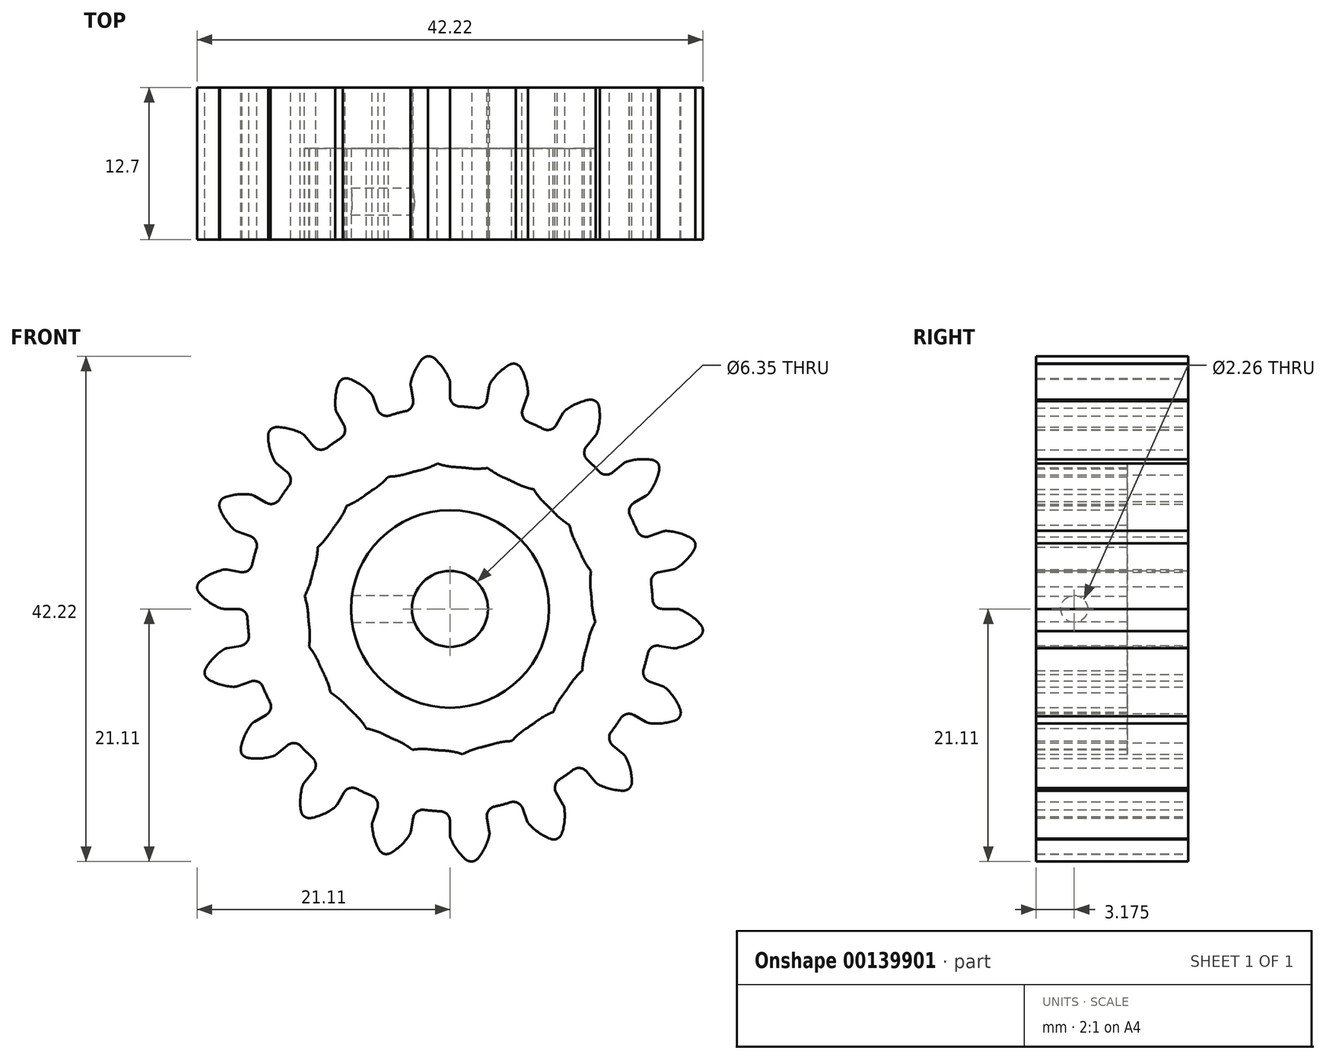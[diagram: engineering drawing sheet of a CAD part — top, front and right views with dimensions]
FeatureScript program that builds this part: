
annotation { "Feature Type Name" : "Feature", "Feature Type Description" : "" }
export const myFeature = defineFeature(function(context is Context, id is Id, definition is map)
    precondition{}
    {
        {
            var Q0;
            Q0=qCreatedBy(makeId("Front.planeOp"),FACE);
            var sketch = newSketch(context, id + "F0", { "sketchPlane" : qUnion([Q0])});
            skArc(sketch, "E0", {"start": v(-3.71, 16.52) * mm, "mid": v(-4.38, 16.35) * mm, "end": v(-5.04, 16.16) * mm});
            skArc(sketch, "E1", {"start": v(-0.07, 19.21) * mm, "mid": v(-0.58, 20.13) * mm, "end": v(-1.28, 20.9) * mm});
            skLineSegment(sketch, "E2", {"start": v(0, 18.89) * mm, "end": v(0, 17.74) * mm});
            skLineSegment(sketch, "E3", {"start": v(-1.83, 21.11) * mm, "end": v(-1.85, 21.11) * mm});
            skLineSegment(sketch, "E4.MirrorCS", {"start": v(-1.86, 21.1) * mm, "end": v(-1.85, 21.11) * mm});
            skArc(sketch, "E5.MirrorCS", {"start": v(-3.27, 18.93) * mm, "mid": v(-2.92, 19.92) * mm, "end": v(-2.37, 20.8) * mm});
            skLineSegment(sketch, "E6.MirrorCS", {"start": v(-3.28, 18.6) * mm, "end": v(-3.08, 17.47) * mm});
            skPoint(sketch, "E7.visualSharp", {"position": v(0, 16.93) * mm});
            skArc(sketch, "E7.filletArc", {"start": v(0, 17.74) * mm, "mid": v(0.23, 17.17) * mm, "end": v(0.79, 16.91) * mm});
            skPoint(sketch, "E8.visualSharp", {"position": v(-2.94, 16.67) * mm});
            skArc(sketch, "E8.filletArc", {"start": v(-3.71, 16.52) * mm, "mid": v(-3.2, 16.86) * mm, "end": v(-3.08, 17.47) * mm});
            skPoint(sketch, "E9.visualSharp", {"position": v(-3.3, 18.76) * mm});
            skArc(sketch, "E9.filletArc", {"start": v(-3.27, 18.93) * mm, "mid": v(-3.3, 18.77) * mm, "end": v(-3.28, 18.6) * mm});
            skPoint(sketch, "E10.visualSharp", {"position": v(0, 19.05) * mm});
            skArc(sketch, "E10.filletArc", {"start": v(0, 18.89) * mm, "mid": v(-0.02, 19.05) * mm, "end": v(-0.07, 19.21) * mm});
            skPoint(sketch, "E11.visualSharp", {"position": v(-2.15, 21.06) * mm});
            skArc(sketch, "E11.filletArc", {"start": v(-1.86, 21.1) * mm, "mid": v(-2.14, 21) * mm, "end": v(-2.37, 20.8) * mm});
            skPoint(sketch, "E12.visualSharp", {"position": v(-1.53, 21.11) * mm});
            skArc(sketch, "E12.filletArc", {"start": v(-1.28, 20.9) * mm, "mid": v(-1.54, 21.06) * mm, "end": v(-1.83, 21.11) * mm});
            skArc(sketch, "E13.1.0", {"start": v(-9.14, 14.25) * mm, "mid": v(-8.78, 14.75) * mm, "end": v(-8.87, 15.36) * mm});
            skLineSegment(sketch, "E13.1.1", {"start": v(-9.44, 16.36) * mm, "end": v(-8.87, 15.36) * mm});
            skArc(sketch, "E13.1.2", {"start": v(-9.55, 16.67) * mm, "mid": v(-9.51, 16.51) * mm, "end": v(-9.44, 16.36) * mm});
            skArc(sketch, "E13.1.3", {"start": v(-9.55, 16.67) * mm, "mid": v(-9.56, 17.72) * mm, "end": v(-9.34, 18.74) * mm});
            skArc(sketch, "E13.1.4", {"start": v(-8.97, 19.2) * mm, "mid": v(-9.2, 19) * mm, "end": v(-9.34, 18.74) * mm});
            skLineSegment(sketch, "E13.1.5", {"start": v(-8.97, 19.2) * mm, "end": v(-8.96, 19.2) * mm});
            skLineSegment(sketch, "E13.1.6", {"start": v(-8.94, 19.21) * mm, "end": v(-8.96, 19.2) * mm});
            skArc(sketch, "E13.1.7", {"start": v(-8.35, 19.2) * mm, "mid": v(-8.65, 19.26) * mm, "end": v(-8.94, 19.21) * mm});
            skArc(sketch, "E13.1.8", {"start": v(-6.63, 18.03) * mm, "mid": v(-7.43, 18.71) * mm, "end": v(-8.35, 19.2) * mm});
            skArc(sketch, "E13.1.9", {"start": v(-6.46, 17.75) * mm, "mid": v(-6.53, 17.9) * mm, "end": v(-6.63, 18.03) * mm});
            skLineSegment(sketch, "E13.1.10", {"start": v(-6.46, 17.75) * mm, "end": v(-6.07, 16.67) * mm});
            skArc(sketch, "E13.1.11", {"start": v(-6.07, 16.67) * mm, "mid": v(-5.66, 16.2) * mm, "end": v(-5.04, 16.16) * mm});
            skArc(sketch, "E13.2.0", {"start": v(-13.46, 10.27) * mm, "mid": v(-13.3, 10.86) * mm, "end": v(-13.59, 11.4) * mm});
            skLineSegment(sketch, "E13.2.1", {"start": v(-14.47, 12.14) * mm, "end": v(-13.59, 11.4) * mm});
            skArc(sketch, "E13.2.2", {"start": v(-14.68, 12.4) * mm, "mid": v(-14.59, 12.26) * mm, "end": v(-14.47, 12.14) * mm});
            skArc(sketch, "E13.2.3", {"start": v(-14.68, 12.4) * mm, "mid": v(-15.04, 13.38) * mm, "end": v(-15.19, 14.42) * mm});
            skArc(sketch, "E13.2.4", {"start": v(-15, 14.97) * mm, "mid": v(-15.14, 14.71) * mm, "end": v(-15.19, 14.42) * mm});
            skLineSegment(sketch, "E13.2.5", {"start": v(-15, 14.97) * mm, "end": v(-14.98, 14.98) * mm});
            skLineSegment(sketch, "E13.2.6", {"start": v(-14.97, 15) * mm, "end": v(-14.98, 14.98) * mm});
            skArc(sketch, "E13.2.7", {"start": v(-14.42, 15.19) * mm, "mid": v(-14.71, 15.14) * mm, "end": v(-14.97, 15) * mm});
            skArc(sketch, "E13.2.8", {"start": v(-12.4, 14.68) * mm, "mid": v(-13.38, 15.04) * mm, "end": v(-14.42, 15.19) * mm});
            skArc(sketch, "E13.2.9", {"start": v(-12.14, 14.47) * mm, "mid": v(-12.26, 14.59) * mm, "end": v(-12.4, 14.68) * mm});
            skLineSegment(sketch, "E13.2.10", {"start": v(-12.14, 14.47) * mm, "end": v(-11.4, 13.59) * mm});
            skArc(sketch, "E13.2.11", {"start": v(-11.4, 13.59) * mm, "mid": v(-10.86, 13.3) * mm, "end": v(-10.27, 13.46) * mm});
            skArc(sketch, "E13.3.0", {"start": v(-16.16, 5.04) * mm, "mid": v(-16.2, 5.66) * mm, "end": v(-16.67, 6.07) * mm});
            skLineSegment(sketch, "E13.3.1", {"start": v(-17.75, 6.46) * mm, "end": v(-16.67, 6.07) * mm});
            skArc(sketch, "E13.3.2", {"start": v(-18.03, 6.63) * mm, "mid": v(-17.9, 6.53) * mm, "end": v(-17.75, 6.46) * mm});
            skArc(sketch, "E13.3.3", {"start": v(-18.03, 6.63) * mm, "mid": v(-18.71, 7.43) * mm, "end": v(-19.2, 8.35) * mm});
            skArc(sketch, "E13.3.4", {"start": v(-19.21, 8.94) * mm, "mid": v(-19.26, 8.65) * mm, "end": v(-19.2, 8.35) * mm});
            skLineSegment(sketch, "E13.3.5", {"start": v(-19.21, 8.94) * mm, "end": v(-19.2, 8.96) * mm});
            skLineSegment(sketch, "E13.3.6", {"start": v(-19.2, 8.97) * mm, "end": v(-19.2, 8.96) * mm});
            skArc(sketch, "E13.3.7", {"start": v(-18.74, 9.34) * mm, "mid": v(-19, 9.2) * mm, "end": v(-19.2, 8.97) * mm});
            skArc(sketch, "E13.3.8", {"start": v(-16.67, 9.55) * mm, "mid": v(-17.72, 9.56) * mm, "end": v(-18.74, 9.34) * mm});
            skArc(sketch, "E13.3.9", {"start": v(-16.36, 9.44) * mm, "mid": v(-16.51, 9.51) * mm, "end": v(-16.67, 9.55) * mm});
            skLineSegment(sketch, "E13.3.10", {"start": v(-16.36, 9.44) * mm, "end": v(-15.36, 8.87) * mm});
            skArc(sketch, "E13.3.11", {"start": v(-15.36, 8.87) * mm, "mid": v(-14.75, 8.78) * mm, "end": v(-14.25, 9.14) * mm});
            skArc(sketch, "E13.4.0", {"start": v(-16.91, -0.79) * mm, "mid": v(-17.17, -0.23) * mm, "end": v(-17.74, 0) * mm});
            skLineSegment(sketch, "E13.4.1", {"start": v(-18.89, 0) * mm, "end": v(-17.74, 0) * mm});
            skArc(sketch, "E13.4.2", {"start": v(-19.21, 0.07) * mm, "mid": v(-19.05, 0.02) * mm, "end": v(-18.89, 0) * mm});
            skArc(sketch, "E13.4.3", {"start": v(-19.21, 0.07) * mm, "mid": v(-20.13, 0.58) * mm, "end": v(-20.9, 1.28) * mm});
            skArc(sketch, "E13.4.4", {"start": v(-21.11, 1.83) * mm, "mid": v(-21.06, 1.54) * mm, "end": v(-20.9, 1.28) * mm});
            skLineSegment(sketch, "E13.4.5", {"start": v(-21.11, 1.83) * mm, "end": v(-21.11, 1.85) * mm});
            skLineSegment(sketch, "E13.4.6", {"start": v(-21.1, 1.86) * mm, "end": v(-21.11, 1.85) * mm});
            skArc(sketch, "E13.4.7", {"start": v(-20.8, 2.37) * mm, "mid": v(-21, 2.14) * mm, "end": v(-21.1, 1.86) * mm});
            skArc(sketch, "E13.4.8", {"start": v(-18.93, 3.27) * mm, "mid": v(-19.92, 2.92) * mm, "end": v(-20.8, 2.37) * mm});
            skArc(sketch, "E13.4.9", {"start": v(-18.6, 3.28) * mm, "mid": v(-18.77, 3.3) * mm, "end": v(-18.93, 3.27) * mm});
            skLineSegment(sketch, "E13.4.10", {"start": v(-18.6, 3.28) * mm, "end": v(-17.47, 3.08) * mm});
            skArc(sketch, "E13.4.11", {"start": v(-17.47, 3.08) * mm, "mid": v(-16.86, 3.2) * mm, "end": v(-16.52, 3.71) * mm});
            skArc(sketch, "E13.5.0", {"start": v(-15.62, -6.52) * mm, "mid": v(-16.05, -6.09) * mm, "end": v(-16.67, -6.07) * mm});
            skLineSegment(sketch, "E13.5.1", {"start": v(-17.75, -6.46) * mm, "end": v(-16.67, -6.07) * mm});
            skArc(sketch, "E13.5.2", {"start": v(-18.08, -6.5) * mm, "mid": v(-17.91, -6.5) * mm, "end": v(-17.75, -6.46) * mm});
            skArc(sketch, "E13.5.3", {"start": v(-18.08, -6.5) * mm, "mid": v(-19.11, -6.34) * mm, "end": v(-20.08, -5.94) * mm});
            skArc(sketch, "E13.5.4", {"start": v(-20.46, -5.5) * mm, "mid": v(-20.31, -5.76) * mm, "end": v(-20.08, -5.94) * mm});
            skLineSegment(sketch, "E13.5.5", {"start": v(-20.46, -5.5) * mm, "end": v(-20.47, -5.48) * mm});
            skLineSegment(sketch, "E13.5.6", {"start": v(-20.47, -5.47) * mm, "end": v(-20.47, -5.48) * mm});
            skArc(sketch, "E13.5.7", {"start": v(-20.36, -4.9) * mm, "mid": v(-20.47, -5.17) * mm, "end": v(-20.47, -5.47) * mm});
            skArc(sketch, "E13.5.8", {"start": v(-18.91, -3.4) * mm, "mid": v(-19.72, -4.07) * mm, "end": v(-20.36, -4.9) * mm});
            skArc(sketch, "E13.5.9", {"start": v(-18.6, -3.28) * mm, "mid": v(-18.76, -3.33) * mm, "end": v(-18.91, -3.4) * mm});
            skLineSegment(sketch, "E13.5.10", {"start": v(-18.6, -3.28) * mm, "end": v(-17.47, -3.08) * mm});
            skArc(sketch, "E13.5.11", {"start": v(-17.47, -3.08) * mm, "mid": v(-16.94, -2.76) * mm, "end": v(-16.8, -2.16) * mm});
            skArc(sketch, "E13.6.0", {"start": v(-12.45, -11.47) * mm, "mid": v(-13, -11.2) * mm, "end": v(-13.59, -11.4) * mm});
            skLineSegment(sketch, "E13.6.1", {"start": v(-14.47, -12.14) * mm, "end": v(-13.59, -11.4) * mm});
            skArc(sketch, "E13.6.2", {"start": v(-14.76, -12.3) * mm, "mid": v(-14.6, -12.24) * mm, "end": v(-14.47, -12.14) * mm});
            skArc(sketch, "E13.6.3", {"start": v(-14.76, -12.3) * mm, "mid": v(-15.8, -12.5) * mm, "end": v(-16.84, -12.45) * mm});
            skArc(sketch, "E13.6.4", {"start": v(-17.35, -12.17) * mm, "mid": v(-17.12, -12.36) * mm, "end": v(-16.84, -12.45) * mm});
            skLineSegment(sketch, "E13.6.5", {"start": v(-17.35, -12.17) * mm, "end": v(-17.36, -12.15) * mm});
            skLineSegment(sketch, "E13.6.6", {"start": v(-17.37, -12.14) * mm, "end": v(-17.36, -12.15) * mm});
            skArc(sketch, "E13.6.7", {"start": v(-17.46, -11.56) * mm, "mid": v(-17.47, -11.86) * mm, "end": v(-17.37, -12.14) * mm});
            skArc(sketch, "E13.6.8", {"start": v(-16.6, -9.66) * mm, "mid": v(-17.14, -10.57) * mm, "end": v(-17.46, -11.56) * mm});
            skArc(sketch, "E13.6.9", {"start": v(-16.36, -9.44) * mm, "mid": v(-16.5, -9.54) * mm, "end": v(-16.6, -9.66) * mm});
            skLineSegment(sketch, "E13.6.10", {"start": v(-16.36, -9.44) * mm, "end": v(-15.36, -8.87) * mm});
            skArc(sketch, "E13.6.11", {"start": v(-15.36, -8.87) * mm, "mid": v(-14.98, -8.38) * mm, "end": v(-15.04, -7.77) * mm});
            skArc(sketch, "E13.7.0", {"start": v(-7.77, -15.04) * mm, "mid": v(-8.38, -14.98) * mm, "end": v(-8.87, -15.36) * mm});
            skLineSegment(sketch, "E13.7.1", {"start": v(-9.44, -16.36) * mm, "end": v(-8.87, -15.36) * mm});
            skArc(sketch, "E13.7.2", {"start": v(-9.66, -16.6) * mm, "mid": v(-9.54, -16.5) * mm, "end": v(-9.44, -16.36) * mm});
            skArc(sketch, "E13.7.3", {"start": v(-9.66, -16.6) * mm, "mid": v(-10.57, -17.14) * mm, "end": v(-11.56, -17.46) * mm});
            skArc(sketch, "E13.7.4", {"start": v(-12.14, -17.37) * mm, "mid": v(-11.86, -17.47) * mm, "end": v(-11.56, -17.46) * mm});
            skLineSegment(sketch, "E13.7.5", {"start": v(-12.14, -17.37) * mm, "end": v(-12.15, -17.36) * mm});
            skLineSegment(sketch, "E13.7.6", {"start": v(-12.17, -17.35) * mm, "end": v(-12.15, -17.36) * mm});
            skArc(sketch, "E13.7.7", {"start": v(-12.45, -16.84) * mm, "mid": v(-12.36, -17.12) * mm, "end": v(-12.17, -17.35) * mm});
            skArc(sketch, "E13.7.8", {"start": v(-12.3, -14.76) * mm, "mid": v(-12.5, -15.8) * mm, "end": v(-12.45, -16.84) * mm});
            skArc(sketch, "E13.7.9", {"start": v(-12.14, -14.47) * mm, "mid": v(-12.24, -14.6) * mm, "end": v(-12.3, -14.76) * mm});
            skLineSegment(sketch, "E13.7.10", {"start": v(-12.14, -14.47) * mm, "end": v(-11.4, -13.59) * mm});
            skArc(sketch, "E13.7.11", {"start": v(-11.4, -13.59) * mm, "mid": v(-11.2, -13) * mm, "end": v(-11.47, -12.45) * mm});
            skArc(sketch, "E13.8.0", {"start": v(-2.16, -16.8) * mm, "mid": v(-2.76, -16.94) * mm, "end": v(-3.08, -17.47) * mm});
            skLineSegment(sketch, "E13.8.1", {"start": v(-3.28, -18.6) * mm, "end": v(-3.08, -17.47) * mm});
            skArc(sketch, "E13.8.2", {"start": v(-3.4, -18.91) * mm, "mid": v(-3.33, -18.76) * mm, "end": v(-3.28, -18.6) * mm});
            skArc(sketch, "E13.8.3", {"start": v(-3.4, -18.91) * mm, "mid": v(-4.07, -19.72) * mm, "end": v(-4.9, -20.36) * mm});
            skArc(sketch, "E13.8.4", {"start": v(-5.47, -20.47) * mm, "mid": v(-5.17, -20.47) * mm, "end": v(-4.9, -20.36) * mm});
            skLineSegment(sketch, "E13.8.5", {"start": v(-5.47, -20.47) * mm, "end": v(-5.48, -20.47) * mm});
            skLineSegment(sketch, "E13.8.6", {"start": v(-5.5, -20.46) * mm, "end": v(-5.48, -20.47) * mm});
            skArc(sketch, "E13.8.7", {"start": v(-5.94, -20.08) * mm, "mid": v(-5.76, -20.31) * mm, "end": v(-5.5, -20.46) * mm});
            skArc(sketch, "E13.8.8", {"start": v(-6.5, -18.08) * mm, "mid": v(-6.34, -19.11) * mm, "end": v(-5.94, -20.08) * mm});
            skArc(sketch, "E13.8.9", {"start": v(-6.46, -17.75) * mm, "mid": v(-6.5, -17.91) * mm, "end": v(-6.5, -18.08) * mm});
            skLineSegment(sketch, "E13.8.10", {"start": v(-6.46, -17.75) * mm, "end": v(-6.07, -16.67) * mm});
            skArc(sketch, "E13.8.11", {"start": v(-6.07, -16.67) * mm, "mid": v(-6.09, -16.05) * mm, "end": v(-6.52, -15.62) * mm});
            skArc(sketch, "E13.9.0", {"start": v(3.71, -16.52) * mm, "mid": v(3.2, -16.86) * mm, "end": v(3.08, -17.47) * mm});
            skLineSegment(sketch, "E13.9.1", {"start": v(3.28, -18.6) * mm, "end": v(3.08, -17.47) * mm});
            skArc(sketch, "E13.9.2", {"start": v(3.27, -18.93) * mm, "mid": v(3.3, -18.77) * mm, "end": v(3.28, -18.6) * mm});
            skArc(sketch, "E13.9.3", {"start": v(3.27, -18.93) * mm, "mid": v(2.92, -19.92) * mm, "end": v(2.37, -20.8) * mm});
            skArc(sketch, "E13.9.4", {"start": v(1.86, -21.1) * mm, "mid": v(2.14, -21) * mm, "end": v(2.37, -20.8) * mm});
            skLineSegment(sketch, "E13.9.5", {"start": v(1.86, -21.1) * mm, "end": v(1.85, -21.11) * mm});
            skLineSegment(sketch, "E13.9.6", {"start": v(1.83, -21.11) * mm, "end": v(1.85, -21.11) * mm});
            skArc(sketch, "E13.9.7", {"start": v(1.28, -20.9) * mm, "mid": v(1.54, -21.06) * mm, "end": v(1.83, -21.11) * mm});
            skArc(sketch, "E13.9.8", {"start": v(0.07, -19.21) * mm, "mid": v(0.58, -20.13) * mm, "end": v(1.28, -20.9) * mm});
            skArc(sketch, "E13.9.9", {"start": v(0, -18.89) * mm, "mid": v(0.02, -19.05) * mm, "end": v(0.07, -19.21) * mm});
            skLineSegment(sketch, "E13.9.10", {"start": v(0, -18.89) * mm, "end": v(0, -17.74) * mm});
            skArc(sketch, "E13.9.11", {"start": v(0, -17.74) * mm, "mid": v(-0.23, -17.17) * mm, "end": v(-0.79, -16.91) * mm});
            skArc(sketch, "E13.10.0", {"start": v(9.14, -14.25) * mm, "mid": v(8.78, -14.75) * mm, "end": v(8.87, -15.36) * mm});
            skLineSegment(sketch, "E13.10.1", {"start": v(9.44, -16.36) * mm, "end": v(8.87, -15.36) * mm});
            skArc(sketch, "E13.10.2", {"start": v(9.55, -16.67) * mm, "mid": v(9.51, -16.51) * mm, "end": v(9.44, -16.36) * mm});
            skArc(sketch, "E13.10.3", {"start": v(9.55, -16.67) * mm, "mid": v(9.56, -17.72) * mm, "end": v(9.34, -18.74) * mm});
            skArc(sketch, "E13.10.4", {"start": v(8.97, -19.2) * mm, "mid": v(9.2, -19) * mm, "end": v(9.34, -18.74) * mm});
            skLineSegment(sketch, "E13.10.5", {"start": v(8.97, -19.2) * mm, "end": v(8.96, -19.2) * mm});
            skLineSegment(sketch, "E13.10.6", {"start": v(8.94, -19.21) * mm, "end": v(8.96, -19.2) * mm});
            skArc(sketch, "E13.10.7", {"start": v(8.35, -19.2) * mm, "mid": v(8.65, -19.26) * mm, "end": v(8.94, -19.21) * mm});
            skArc(sketch, "E13.10.8", {"start": v(6.63, -18.03) * mm, "mid": v(7.43, -18.71) * mm, "end": v(8.35, -19.2) * mm});
            skArc(sketch, "E13.10.9", {"start": v(6.46, -17.75) * mm, "mid": v(6.53, -17.9) * mm, "end": v(6.63, -18.03) * mm});
            skLineSegment(sketch, "E13.10.10", {"start": v(6.46, -17.75) * mm, "end": v(6.07, -16.67) * mm});
            skArc(sketch, "E13.10.11", {"start": v(6.07, -16.67) * mm, "mid": v(5.66, -16.2) * mm, "end": v(5.04, -16.16) * mm});
            skArc(sketch, "E13.11.0", {"start": v(13.46, -10.27) * mm, "mid": v(13.3, -10.86) * mm, "end": v(13.59, -11.4) * mm});
            skLineSegment(sketch, "E13.11.1", {"start": v(14.47, -12.14) * mm, "end": v(13.59, -11.4) * mm});
            skArc(sketch, "E13.11.2", {"start": v(14.68, -12.4) * mm, "mid": v(14.59, -12.26) * mm, "end": v(14.47, -12.14) * mm});
            skArc(sketch, "E13.11.3", {"start": v(14.68, -12.4) * mm, "mid": v(15.04, -13.38) * mm, "end": v(15.19, -14.42) * mm});
            skArc(sketch, "E13.11.4", {"start": v(15, -14.97) * mm, "mid": v(15.14, -14.71) * mm, "end": v(15.19, -14.42) * mm});
            skLineSegment(sketch, "E13.11.5", {"start": v(15, -14.97) * mm, "end": v(14.98, -14.98) * mm});
            skLineSegment(sketch, "E13.11.6", {"start": v(14.97, -15) * mm, "end": v(14.98, -14.98) * mm});
            skArc(sketch, "E13.11.7", {"start": v(14.42, -15.19) * mm, "mid": v(14.71, -15.14) * mm, "end": v(14.97, -15) * mm});
            skArc(sketch, "E13.11.8", {"start": v(12.4, -14.68) * mm, "mid": v(13.38, -15.04) * mm, "end": v(14.42, -15.19) * mm});
            skArc(sketch, "E13.11.9", {"start": v(12.14, -14.47) * mm, "mid": v(12.26, -14.59) * mm, "end": v(12.4, -14.68) * mm});
            skLineSegment(sketch, "E13.11.10", {"start": v(12.14, -14.47) * mm, "end": v(11.4, -13.59) * mm});
            skArc(sketch, "E13.11.11", {"start": v(11.4, -13.59) * mm, "mid": v(10.86, -13.3) * mm, "end": v(10.27, -13.46) * mm});
            skArc(sketch, "E13.12.0", {"start": v(16.16, -5.04) * mm, "mid": v(16.2, -5.66) * mm, "end": v(16.67, -6.07) * mm});
            skLineSegment(sketch, "E13.12.1", {"start": v(17.75, -6.46) * mm, "end": v(16.67, -6.07) * mm});
            skArc(sketch, "E13.12.2", {"start": v(18.03, -6.63) * mm, "mid": v(17.9, -6.53) * mm, "end": v(17.75, -6.46) * mm});
            skArc(sketch, "E13.12.3", {"start": v(18.03, -6.63) * mm, "mid": v(18.71, -7.43) * mm, "end": v(19.2, -8.35) * mm});
            skArc(sketch, "E13.12.4", {"start": v(19.21, -8.94) * mm, "mid": v(19.26, -8.65) * mm, "end": v(19.2, -8.35) * mm});
            skLineSegment(sketch, "E13.12.5", {"start": v(19.21, -8.94) * mm, "end": v(19.2, -8.96) * mm});
            skLineSegment(sketch, "E13.12.6", {"start": v(19.2, -8.97) * mm, "end": v(19.2, -8.96) * mm});
            skArc(sketch, "E13.12.7", {"start": v(18.74, -9.34) * mm, "mid": v(19, -9.2) * mm, "end": v(19.2, -8.97) * mm});
            skArc(sketch, "E13.12.8", {"start": v(16.67, -9.55) * mm, "mid": v(17.72, -9.56) * mm, "end": v(18.74, -9.34) * mm});
            skArc(sketch, "E13.12.9", {"start": v(16.36, -9.44) * mm, "mid": v(16.51, -9.51) * mm, "end": v(16.67, -9.55) * mm});
            skLineSegment(sketch, "E13.12.10", {"start": v(16.36, -9.44) * mm, "end": v(15.36, -8.87) * mm});
            skArc(sketch, "E13.12.11", {"start": v(15.36, -8.87) * mm, "mid": v(14.75, -8.78) * mm, "end": v(14.25, -9.14) * mm});
            skArc(sketch, "E13.13.0", {"start": v(16.91, 0.79) * mm, "mid": v(17.17, 0.23) * mm, "end": v(17.74, 0) * mm});
            skLineSegment(sketch, "E13.13.1", {"start": v(18.89, 0) * mm, "end": v(17.74, 0) * mm});
            skArc(sketch, "E13.13.2", {"start": v(19.21, -0.07) * mm, "mid": v(19.05, -0.02) * mm, "end": v(18.89, 0) * mm});
            skArc(sketch, "E13.13.3", {"start": v(19.21, -0.07) * mm, "mid": v(20.13, -0.58) * mm, "end": v(20.9, -1.28) * mm});
            skArc(sketch, "E13.13.4", {"start": v(21.11, -1.83) * mm, "mid": v(21.06, -1.54) * mm, "end": v(20.9, -1.28) * mm});
            skLineSegment(sketch, "E13.13.5", {"start": v(21.11, -1.83) * mm, "end": v(21.11, -1.85) * mm});
            skLineSegment(sketch, "E13.13.6", {"start": v(21.1, -1.86) * mm, "end": v(21.11, -1.85) * mm});
            skArc(sketch, "E13.13.7", {"start": v(20.8, -2.37) * mm, "mid": v(21, -2.14) * mm, "end": v(21.1, -1.86) * mm});
            skArc(sketch, "E13.13.8", {"start": v(18.93, -3.27) * mm, "mid": v(19.92, -2.92) * mm, "end": v(20.8, -2.37) * mm});
            skArc(sketch, "E13.13.9", {"start": v(18.6, -3.28) * mm, "mid": v(18.77, -3.3) * mm, "end": v(18.93, -3.27) * mm});
            skLineSegment(sketch, "E13.13.10", {"start": v(18.6, -3.28) * mm, "end": v(17.47, -3.08) * mm});
            skArc(sketch, "E13.13.11", {"start": v(17.47, -3.08) * mm, "mid": v(16.86, -3.2) * mm, "end": v(16.52, -3.71) * mm});
            skArc(sketch, "E13.14.0", {"start": v(15.62, 6.52) * mm, "mid": v(16.05, 6.09) * mm, "end": v(16.67, 6.07) * mm});
            skLineSegment(sketch, "E13.14.1", {"start": v(17.75, 6.46) * mm, "end": v(16.67, 6.07) * mm});
            skArc(sketch, "E13.14.2", {"start": v(18.08, 6.5) * mm, "mid": v(17.91, 6.5) * mm, "end": v(17.75, 6.46) * mm});
            skArc(sketch, "E13.14.3", {"start": v(18.08, 6.5) * mm, "mid": v(19.11, 6.34) * mm, "end": v(20.08, 5.94) * mm});
            skArc(sketch, "E13.14.4", {"start": v(20.46, 5.5) * mm, "mid": v(20.31, 5.76) * mm, "end": v(20.08, 5.94) * mm});
            skLineSegment(sketch, "E13.14.5", {"start": v(20.46, 5.5) * mm, "end": v(20.47, 5.48) * mm});
            skLineSegment(sketch, "E13.14.6", {"start": v(20.47, 5.47) * mm, "end": v(20.47, 5.48) * mm});
            skArc(sketch, "E13.14.7", {"start": v(20.36, 4.9) * mm, "mid": v(20.47, 5.17) * mm, "end": v(20.47, 5.47) * mm});
            skArc(sketch, "E13.14.8", {"start": v(18.91, 3.4) * mm, "mid": v(19.72, 4.07) * mm, "end": v(20.36, 4.9) * mm});
            skArc(sketch, "E13.14.9", {"start": v(18.6, 3.28) * mm, "mid": v(18.76, 3.33) * mm, "end": v(18.91, 3.4) * mm});
            skLineSegment(sketch, "E13.14.10", {"start": v(18.6, 3.28) * mm, "end": v(17.47, 3.08) * mm});
            skArc(sketch, "E13.14.11", {"start": v(17.47, 3.08) * mm, "mid": v(16.94, 2.76) * mm, "end": v(16.8, 2.16) * mm});
            skArc(sketch, "E13.15.0", {"start": v(12.45, 11.47) * mm, "mid": v(13, 11.2) * mm, "end": v(13.59, 11.4) * mm});
            skLineSegment(sketch, "E13.15.1", {"start": v(14.47, 12.14) * mm, "end": v(13.59, 11.4) * mm});
            skArc(sketch, "E13.15.2", {"start": v(14.76, 12.3) * mm, "mid": v(14.6, 12.24) * mm, "end": v(14.47, 12.14) * mm});
            skArc(sketch, "E13.15.3", {"start": v(14.76, 12.3) * mm, "mid": v(15.8, 12.5) * mm, "end": v(16.84, 12.45) * mm});
            skArc(sketch, "E13.15.4", {"start": v(17.35, 12.17) * mm, "mid": v(17.12, 12.36) * mm, "end": v(16.84, 12.45) * mm});
            skLineSegment(sketch, "E13.15.5", {"start": v(17.35, 12.17) * mm, "end": v(17.36, 12.15) * mm});
            skLineSegment(sketch, "E13.15.6", {"start": v(17.37, 12.14) * mm, "end": v(17.36, 12.15) * mm});
            skArc(sketch, "E13.15.7", {"start": v(17.46, 11.56) * mm, "mid": v(17.47, 11.86) * mm, "end": v(17.37, 12.14) * mm});
            skArc(sketch, "E13.15.8", {"start": v(16.6, 9.66) * mm, "mid": v(17.14, 10.57) * mm, "end": v(17.46, 11.56) * mm});
            skArc(sketch, "E13.15.9", {"start": v(16.36, 9.44) * mm, "mid": v(16.5, 9.54) * mm, "end": v(16.6, 9.66) * mm});
            skLineSegment(sketch, "E13.15.10", {"start": v(16.36, 9.44) * mm, "end": v(15.36, 8.87) * mm});
            skArc(sketch, "E13.15.11", {"start": v(15.36, 8.87) * mm, "mid": v(14.98, 8.38) * mm, "end": v(15.04, 7.77) * mm});
            skArc(sketch, "E13.16.0", {"start": v(7.77, 15.04) * mm, "mid": v(8.38, 14.98) * mm, "end": v(8.87, 15.36) * mm});
            skLineSegment(sketch, "E13.16.1", {"start": v(9.44, 16.36) * mm, "end": v(8.87, 15.36) * mm});
            skArc(sketch, "E13.16.2", {"start": v(9.66, 16.6) * mm, "mid": v(9.54, 16.5) * mm, "end": v(9.44, 16.36) * mm});
            skArc(sketch, "E13.16.3", {"start": v(9.66, 16.6) * mm, "mid": v(10.57, 17.14) * mm, "end": v(11.56, 17.46) * mm});
            skArc(sketch, "E13.16.4", {"start": v(12.14, 17.37) * mm, "mid": v(11.86, 17.47) * mm, "end": v(11.56, 17.46) * mm});
            skLineSegment(sketch, "E13.16.5", {"start": v(12.14, 17.37) * mm, "end": v(12.15, 17.36) * mm});
            skLineSegment(sketch, "E13.16.6", {"start": v(12.17, 17.35) * mm, "end": v(12.15, 17.36) * mm});
            skArc(sketch, "E13.16.7", {"start": v(12.45, 16.84) * mm, "mid": v(12.36, 17.12) * mm, "end": v(12.17, 17.35) * mm});
            skArc(sketch, "E13.16.8", {"start": v(12.3, 14.76) * mm, "mid": v(12.5, 15.8) * mm, "end": v(12.45, 16.84) * mm});
            skArc(sketch, "E13.16.9", {"start": v(12.14, 14.47) * mm, "mid": v(12.24, 14.6) * mm, "end": v(12.3, 14.76) * mm});
            skLineSegment(sketch, "E13.16.10", {"start": v(12.14, 14.47) * mm, "end": v(11.4, 13.59) * mm});
            skArc(sketch, "E13.16.11", {"start": v(11.4, 13.59) * mm, "mid": v(11.2, 13) * mm, "end": v(11.47, 12.45) * mm});
            skArc(sketch, "E13.17.0", {"start": v(2.16, 16.8) * mm, "mid": v(2.76, 16.94) * mm, "end": v(3.08, 17.47) * mm});
            skLineSegment(sketch, "E13.17.1", {"start": v(3.28, 18.6) * mm, "end": v(3.08, 17.47) * mm});
            skArc(sketch, "E13.17.2", {"start": v(3.4, 18.91) * mm, "mid": v(3.33, 18.76) * mm, "end": v(3.28, 18.6) * mm});
            skArc(sketch, "E13.17.3", {"start": v(3.4, 18.91) * mm, "mid": v(4.07, 19.72) * mm, "end": v(4.9, 20.36) * mm});
            skArc(sketch, "E13.17.4", {"start": v(5.47, 20.47) * mm, "mid": v(5.17, 20.47) * mm, "end": v(4.9, 20.36) * mm});
            skLineSegment(sketch, "E13.17.5", {"start": v(5.47, 20.47) * mm, "end": v(5.48, 20.47) * mm});
            skLineSegment(sketch, "E13.17.6", {"start": v(5.5, 20.46) * mm, "end": v(5.48, 20.47) * mm});
            skArc(sketch, "E13.17.7", {"start": v(5.94, 20.08) * mm, "mid": v(5.76, 20.31) * mm, "end": v(5.5, 20.46) * mm});
            skArc(sketch, "E13.17.8", {"start": v(6.5, 18.08) * mm, "mid": v(6.34, 19.11) * mm, "end": v(5.94, 20.08) * mm});
            skArc(sketch, "E13.17.9", {"start": v(6.46, 17.75) * mm, "mid": v(6.5, 17.91) * mm, "end": v(6.5, 18.08) * mm});
            skLineSegment(sketch, "E13.17.10", {"start": v(6.46, 17.75) * mm, "end": v(6.07, 16.67) * mm});
            skArc(sketch, "E13.17.11", {"start": v(6.07, 16.67) * mm, "mid": v(6.09, 16.05) * mm, "end": v(6.52, 15.62) * mm});
            skArc(sketch, "E14.trimOffspring", {"start": v(-9.14, 14.25) * mm, "mid": v(-9.71, 13.87) * mm, "end": v(-10.27, 13.46) * mm});
            skArc(sketch, "E15.trimOffspring", {"start": v(-13.46, 10.27) * mm, "mid": v(-13.87, 9.71) * mm, "end": v(-14.25, 9.14) * mm});
            skArc(sketch, "E16.trimOffspring", {"start": v(-16.16, 5.04) * mm, "mid": v(-16.35, 4.38) * mm, "end": v(-16.52, 3.71) * mm});
            skArc(sketch, "E17.trimOffspring", {"start": v(-16.91, -0.79) * mm, "mid": v(-16.86, -1.48) * mm, "end": v(-16.8, -2.16) * mm});
            skArc(sketch, "E18.trimOffspring", {"start": v(-15.62, -6.52) * mm, "mid": v(-15.34, -7.15) * mm, "end": v(-15.04, -7.77) * mm});
            skArc(sketch, "E19.trimOffspring", {"start": v(-12.45, -11.47) * mm, "mid": v(-11.97, -11.97) * mm, "end": v(-11.47, -12.45) * mm});
            skArc(sketch, "E20.trimOffspring", {"start": v(-7.77, -15.04) * mm, "mid": v(-7.15, -15.34) * mm, "end": v(-6.52, -15.62) * mm});
            skArc(sketch, "E21.trimOffspring", {"start": v(-2.16, -16.8) * mm, "mid": v(-1.48, -16.86) * mm, "end": v(-0.79, -16.91) * mm});
            skArc(sketch, "E22.trimOffspring", {"start": v(3.71, -16.52) * mm, "mid": v(4.38, -16.35) * mm, "end": v(5.04, -16.16) * mm});
            skArc(sketch, "E23.trimOffspring", {"start": v(9.14, -14.25) * mm, "mid": v(9.71, -13.87) * mm, "end": v(10.27, -13.46) * mm});
            skArc(sketch, "E24.trimOffspring", {"start": v(13.46, -10.27) * mm, "mid": v(13.87, -9.71) * mm, "end": v(14.25, -9.14) * mm});
            skArc(sketch, "E25.trimOffspring", {"start": v(16.16, -5.04) * mm, "mid": v(16.35, -4.38) * mm, "end": v(16.52, -3.71) * mm});
            skArc(sketch, "E26.trimOffspring", {"start": v(16.91, 0.79) * mm, "mid": v(16.86, 1.48) * mm, "end": v(16.8, 2.16) * mm});
            skArc(sketch, "E27.trimOffspring", {"start": v(15.62, 6.52) * mm, "mid": v(15.34, 7.15) * mm, "end": v(15.04, 7.77) * mm});
            skArc(sketch, "E28.trimOffspring", {"start": v(12.45, 11.47) * mm, "mid": v(11.97, 11.97) * mm, "end": v(11.47, 12.45) * mm});
            skArc(sketch, "E29.trimOffspring", {"start": v(7.77, 15.04) * mm, "mid": v(7.15, 15.34) * mm, "end": v(6.52, 15.62) * mm});
            skArc(sketch, "E30.trimOffspring", {"start": v(2.16, 16.8) * mm, "mid": v(1.48, 16.86) * mm, "end": v(0.79, 16.91) * mm});
            skSolve(sketch);
        }
        {
            var Q0;
            Q0=makeQuery(id+"F0.imprint","IMPRINT",FACE,{"disambiguationData":[TD([[makeQuery(id+"F0.imprint","IMPRINT",EDGE,{"derivedFrom":sQuery(id+"F0.wireOp",EDGE,"E0")}),1.0]])]});
            extrude(context, id + "F1", {"entities" : qUnion([Q0]), "depth" : 12.7 * mm});
        }
        {
            var Q0;
            Q0=makeQuery(id+"F1.opExtrude","CAP_FACE",FACE,{"disambiguationData":[OSD([sQuery(id+"F0.wireOp",EDGE,"E0"),sQuery(id+"F0.wireOp",EDGE,"E1"),sQuery(id+"F0.wireOp",EDGE,"E2"),sQuery(id+"F0.wireOp",EDGE,"E3"),sQuery(id+"F0.wireOp",EDGE,"E4.MirrorCS"),sQuery(id+"F0.wireOp",EDGE,"E5.MirrorCS"),sQuery(id+"F0.wireOp",EDGE,"E6.MirrorCS"),sQuery(id+"F0.wireOp",EDGE,"E7.filletArc"),sQuery(id+"F0.wireOp",EDGE,"E8.filletArc"),sQuery(id+"F0.wireOp",EDGE,"E9.filletArc"),sQuery(id+"F0.wireOp",EDGE,"E10.filletArc"),sQuery(id+"F0.wireOp",EDGE,"E11.filletArc"),sQuery(id+"F0.wireOp",EDGE,"E12.filletArc"),sQuery(id+"F0.wireOp",EDGE,"E13.1.0"),sQuery(id+"F0.wireOp",EDGE,"E13.1.1"),sQuery(id+"F0.wireOp",EDGE,"E13.1.2"),sQuery(id+"F0.wireOp",EDGE,"E13.1.3"),sQuery(id+"F0.wireOp",EDGE,"E13.1.4"),sQuery(id+"F0.wireOp",EDGE,"E13.1.5"),sQuery(id+"F0.wireOp",EDGE,"E13.1.6"),sQuery(id+"F0.wireOp",EDGE,"E13.1.7"),sQuery(id+"F0.wireOp",EDGE,"E13.1.8"),sQuery(id+"F0.wireOp",EDGE,"E13.1.9"),sQuery(id+"F0.wireOp",EDGE,"E13.1.10"),sQuery(id+"F0.wireOp",EDGE,"E13.1.11"),sQuery(id+"F0.wireOp",EDGE,"E13.2.0"),sQuery(id+"F0.wireOp",EDGE,"E13.2.1"),sQuery(id+"F0.wireOp",EDGE,"E13.2.2"),sQuery(id+"F0.wireOp",EDGE,"E13.2.3"),sQuery(id+"F0.wireOp",EDGE,"E13.2.4"),sQuery(id+"F0.wireOp",EDGE,"E13.2.5"),sQuery(id+"F0.wireOp",EDGE,"E13.2.6"),sQuery(id+"F0.wireOp",EDGE,"E13.2.7"),sQuery(id+"F0.wireOp",EDGE,"E13.2.8"),sQuery(id+"F0.wireOp",EDGE,"E13.2.9"),sQuery(id+"F0.wireOp",EDGE,"E13.2.10"),sQuery(id+"F0.wireOp",EDGE,"E13.2.11"),sQuery(id+"F0.wireOp",EDGE,"E13.3.0"),sQuery(id+"F0.wireOp",EDGE,"E13.3.1"),sQuery(id+"F0.wireOp",EDGE,"E13.3.2"),sQuery(id+"F0.wireOp",EDGE,"E13.3.3"),sQuery(id+"F0.wireOp",EDGE,"E13.3.4"),sQuery(id+"F0.wireOp",EDGE,"E13.3.5"),sQuery(id+"F0.wireOp",EDGE,"E13.3.6"),sQuery(id+"F0.wireOp",EDGE,"E13.3.7"),sQuery(id+"F0.wireOp",EDGE,"E13.3.8"),sQuery(id+"F0.wireOp",EDGE,"E13.3.9"),sQuery(id+"F0.wireOp",EDGE,"E13.3.10"),sQuery(id+"F0.wireOp",EDGE,"E13.3.11"),sQuery(id+"F0.wireOp",EDGE,"E13.4.0"),sQuery(id+"F0.wireOp",EDGE,"E13.4.1"),sQuery(id+"F0.wireOp",EDGE,"E13.4.2"),sQuery(id+"F0.wireOp",EDGE,"E13.4.3"),sQuery(id+"F0.wireOp",EDGE,"E13.4.4"),sQuery(id+"F0.wireOp",EDGE,"E13.4.5"),sQuery(id+"F0.wireOp",EDGE,"E13.4.6"),sQuery(id+"F0.wireOp",EDGE,"E13.4.7"),sQuery(id+"F0.wireOp",EDGE,"E13.4.8"),sQuery(id+"F0.wireOp",EDGE,"E13.4.9"),sQuery(id+"F0.wireOp",EDGE,"E13.4.10"),sQuery(id+"F0.wireOp",EDGE,"E13.4.11"),sQuery(id+"F0.wireOp",EDGE,"E13.5.0"),sQuery(id+"F0.wireOp",EDGE,"E13.5.1"),sQuery(id+"F0.wireOp",EDGE,"E13.5.2"),sQuery(id+"F0.wireOp",EDGE,"E13.5.3"),sQuery(id+"F0.wireOp",EDGE,"E13.5.4"),sQuery(id+"F0.wireOp",EDGE,"E13.5.5"),sQuery(id+"F0.wireOp",EDGE,"E13.5.6"),sQuery(id+"F0.wireOp",EDGE,"E13.5.7"),sQuery(id+"F0.wireOp",EDGE,"E13.5.8"),sQuery(id+"F0.wireOp",EDGE,"E13.5.9"),sQuery(id+"F0.wireOp",EDGE,"E13.5.10"),sQuery(id+"F0.wireOp",EDGE,"E13.5.11"),sQuery(id+"F0.wireOp",EDGE,"E13.6.0"),sQuery(id+"F0.wireOp",EDGE,"E13.6.1"),sQuery(id+"F0.wireOp",EDGE,"E13.6.2"),sQuery(id+"F0.wireOp",EDGE,"E13.6.3"),sQuery(id+"F0.wireOp",EDGE,"E13.6.4"),sQuery(id+"F0.wireOp",EDGE,"E13.6.5"),sQuery(id+"F0.wireOp",EDGE,"E13.6.6"),sQuery(id+"F0.wireOp",EDGE,"E13.6.7"),sQuery(id+"F0.wireOp",EDGE,"E13.6.8"),sQuery(id+"F0.wireOp",EDGE,"E13.6.9"),sQuery(id+"F0.wireOp",EDGE,"E13.6.10"),sQuery(id+"F0.wireOp",EDGE,"E13.6.11"),sQuery(id+"F0.wireOp",EDGE,"E13.7.0"),sQuery(id+"F0.wireOp",EDGE,"E13.7.1"),sQuery(id+"F0.wireOp",EDGE,"E13.7.2"),sQuery(id+"F0.wireOp",EDGE,"E13.7.3"),sQuery(id+"F0.wireOp",EDGE,"E13.7.4"),sQuery(id+"F0.wireOp",EDGE,"E13.7.5"),sQuery(id+"F0.wireOp",EDGE,"E13.7.6"),sQuery(id+"F0.wireOp",EDGE,"E13.7.7"),sQuery(id+"F0.wireOp",EDGE,"E13.7.8"),sQuery(id+"F0.wireOp",EDGE,"E13.7.9"),sQuery(id+"F0.wireOp",EDGE,"E13.7.10"),sQuery(id+"F0.wireOp",EDGE,"E13.7.11"),sQuery(id+"F0.wireOp",EDGE,"E13.8.0"),sQuery(id+"F0.wireOp",EDGE,"E13.8.1"),sQuery(id+"F0.wireOp",EDGE,"E13.8.2"),sQuery(id+"F0.wireOp",EDGE,"E13.8.3"),sQuery(id+"F0.wireOp",EDGE,"E13.8.4"),sQuery(id+"F0.wireOp",EDGE,"E13.8.5"),sQuery(id+"F0.wireOp",EDGE,"E13.8.6"),sQuery(id+"F0.wireOp",EDGE,"E13.8.7"),sQuery(id+"F0.wireOp",EDGE,"E13.8.8"),sQuery(id+"F0.wireOp",EDGE,"E13.8.9"),sQuery(id+"F0.wireOp",EDGE,"E13.8.10"),sQuery(id+"F0.wireOp",EDGE,"E13.8.11"),sQuery(id+"F0.wireOp",EDGE,"E13.9.0"),sQuery(id+"F0.wireOp",EDGE,"E13.9.1"),sQuery(id+"F0.wireOp",EDGE,"E13.9.2"),sQuery(id+"F0.wireOp",EDGE,"E13.9.3"),sQuery(id+"F0.wireOp",EDGE,"E13.9.4"),sQuery(id+"F0.wireOp",EDGE,"E13.9.5"),sQuery(id+"F0.wireOp",EDGE,"E13.9.6"),sQuery(id+"F0.wireOp",EDGE,"E13.9.7"),sQuery(id+"F0.wireOp",EDGE,"E13.9.8"),sQuery(id+"F0.wireOp",EDGE,"E13.9.9"),sQuery(id+"F0.wireOp",EDGE,"E13.9.10"),sQuery(id+"F0.wireOp",EDGE,"E13.9.11"),sQuery(id+"F0.wireOp",EDGE,"E13.10.0"),sQuery(id+"F0.wireOp",EDGE,"E13.10.1"),sQuery(id+"F0.wireOp",EDGE,"E13.10.2"),sQuery(id+"F0.wireOp",EDGE,"E13.10.3"),sQuery(id+"F0.wireOp",EDGE,"E13.10.4"),sQuery(id+"F0.wireOp",EDGE,"E13.10.5"),sQuery(id+"F0.wireOp",EDGE,"E13.10.6"),sQuery(id+"F0.wireOp",EDGE,"E13.10.7"),sQuery(id+"F0.wireOp",EDGE,"E13.10.8"),sQuery(id+"F0.wireOp",EDGE,"E13.10.9"),sQuery(id+"F0.wireOp",EDGE,"E13.10.10"),sQuery(id+"F0.wireOp",EDGE,"E13.10.11"),sQuery(id+"F0.wireOp",EDGE,"E13.11.0"),sQuery(id+"F0.wireOp",EDGE,"E13.11.1"),sQuery(id+"F0.wireOp",EDGE,"E13.11.2"),sQuery(id+"F0.wireOp",EDGE,"E13.11.3"),sQuery(id+"F0.wireOp",EDGE,"E13.11.4"),sQuery(id+"F0.wireOp",EDGE,"E13.11.5"),sQuery(id+"F0.wireOp",EDGE,"E13.11.6"),sQuery(id+"F0.wireOp",EDGE,"E13.11.7"),sQuery(id+"F0.wireOp",EDGE,"E13.11.8"),sQuery(id+"F0.wireOp",EDGE,"E13.11.9"),sQuery(id+"F0.wireOp",EDGE,"E13.11.10"),sQuery(id+"F0.wireOp",EDGE,"E13.11.11"),sQuery(id+"F0.wireOp",EDGE,"E13.12.0"),sQuery(id+"F0.wireOp",EDGE,"E13.12.1"),sQuery(id+"F0.wireOp",EDGE,"E13.12.2"),sQuery(id+"F0.wireOp",EDGE,"E13.12.3"),sQuery(id+"F0.wireOp",EDGE,"E13.12.4"),sQuery(id+"F0.wireOp",EDGE,"E13.12.5"),sQuery(id+"F0.wireOp",EDGE,"E13.12.6"),sQuery(id+"F0.wireOp",EDGE,"E13.12.7"),sQuery(id+"F0.wireOp",EDGE,"E13.12.8"),sQuery(id+"F0.wireOp",EDGE,"E13.12.9"),sQuery(id+"F0.wireOp",EDGE,"E13.12.10"),sQuery(id+"F0.wireOp",EDGE,"E13.12.11"),sQuery(id+"F0.wireOp",EDGE,"E13.13.0"),sQuery(id+"F0.wireOp",EDGE,"E13.13.1"),sQuery(id+"F0.wireOp",EDGE,"E13.13.2"),sQuery(id+"F0.wireOp",EDGE,"E13.13.3"),sQuery(id+"F0.wireOp",EDGE,"E13.13.4"),sQuery(id+"F0.wireOp",EDGE,"E13.13.5"),sQuery(id+"F0.wireOp",EDGE,"E13.13.6"),sQuery(id+"F0.wireOp",EDGE,"E13.13.7"),sQuery(id+"F0.wireOp",EDGE,"E13.13.8"),sQuery(id+"F0.wireOp",EDGE,"E13.13.9"),sQuery(id+"F0.wireOp",EDGE,"E13.13.10"),sQuery(id+"F0.wireOp",EDGE,"E13.13.11"),sQuery(id+"F0.wireOp",EDGE,"E13.14.0"),sQuery(id+"F0.wireOp",EDGE,"E13.14.1"),sQuery(id+"F0.wireOp",EDGE,"E13.14.2"),sQuery(id+"F0.wireOp",EDGE,"E13.14.3"),sQuery(id+"F0.wireOp",EDGE,"E13.14.4"),sQuery(id+"F0.wireOp",EDGE,"E13.14.5"),sQuery(id+"F0.wireOp",EDGE,"E13.14.6"),sQuery(id+"F0.wireOp",EDGE,"E13.14.7"),sQuery(id+"F0.wireOp",EDGE,"E13.14.8"),sQuery(id+"F0.wireOp",EDGE,"E13.14.9"),sQuery(id+"F0.wireOp",EDGE,"E13.14.10"),sQuery(id+"F0.wireOp",EDGE,"E13.14.11"),sQuery(id+"F0.wireOp",EDGE,"E13.15.0"),sQuery(id+"F0.wireOp",EDGE,"E13.15.1"),sQuery(id+"F0.wireOp",EDGE,"E13.15.2"),sQuery(id+"F0.wireOp",EDGE,"E13.15.3"),sQuery(id+"F0.wireOp",EDGE,"E13.15.4"),sQuery(id+"F0.wireOp",EDGE,"E13.15.5"),sQuery(id+"F0.wireOp",EDGE,"E13.15.6"),sQuery(id+"F0.wireOp",EDGE,"E13.15.7"),sQuery(id+"F0.wireOp",EDGE,"E13.15.8"),sQuery(id+"F0.wireOp",EDGE,"E13.15.9"),sQuery(id+"F0.wireOp",EDGE,"E13.15.10"),sQuery(id+"F0.wireOp",EDGE,"E13.15.11"),sQuery(id+"F0.wireOp",EDGE,"E13.16.0"),sQuery(id+"F0.wireOp",EDGE,"E13.16.1"),sQuery(id+"F0.wireOp",EDGE,"E13.16.2"),sQuery(id+"F0.wireOp",EDGE,"E13.16.3"),sQuery(id+"F0.wireOp",EDGE,"E13.16.4"),sQuery(id+"F0.wireOp",EDGE,"E13.16.5"),sQuery(id+"F0.wireOp",EDGE,"E13.16.6"),sQuery(id+"F0.wireOp",EDGE,"E13.16.7"),sQuery(id+"F0.wireOp",EDGE,"E13.16.8"),sQuery(id+"F0.wireOp",EDGE,"E13.16.9"),sQuery(id+"F0.wireOp",EDGE,"E13.16.10"),sQuery(id+"F0.wireOp",EDGE,"E13.16.11"),sQuery(id+"F0.wireOp",EDGE,"E13.17.0"),sQuery(id+"F0.wireOp",EDGE,"E13.17.1"),sQuery(id+"F0.wireOp",EDGE,"E13.17.2"),sQuery(id+"F0.wireOp",EDGE,"E13.17.3"),sQuery(id+"F0.wireOp",EDGE,"E13.17.4"),sQuery(id+"F0.wireOp",EDGE,"E13.17.5"),sQuery(id+"F0.wireOp",EDGE,"E13.17.6"),sQuery(id+"F0.wireOp",EDGE,"E13.17.7"),sQuery(id+"F0.wireOp",EDGE,"E13.17.8"),sQuery(id+"F0.wireOp",EDGE,"E13.17.9"),sQuery(id+"F0.wireOp",EDGE,"E13.17.10"),sQuery(id+"F0.wireOp",EDGE,"E13.17.11"),sQuery(id+"F0.wireOp",EDGE,"E14.trimOffspring"),sQuery(id+"F0.wireOp",EDGE,"E15.trimOffspring"),sQuery(id+"F0.wireOp",EDGE,"E16.trimOffspring"),sQuery(id+"F0.wireOp",EDGE,"E17.trimOffspring"),sQuery(id+"F0.wireOp",EDGE,"E18.trimOffspring"),sQuery(id+"F0.wireOp",EDGE,"E19.trimOffspring"),sQuery(id+"F0.wireOp",EDGE,"E20.trimOffspring"),sQuery(id+"F0.wireOp",EDGE,"E21.trimOffspring"),sQuery(id+"F0.wireOp",EDGE,"E22.trimOffspring"),sQuery(id+"F0.wireOp",EDGE,"E23.trimOffspring"),sQuery(id+"F0.wireOp",EDGE,"E24.trimOffspring"),sQuery(id+"F0.wireOp",EDGE,"E25.trimOffspring"),sQuery(id+"F0.wireOp",EDGE,"E26.trimOffspring"),sQuery(id+"F0.wireOp",EDGE,"E27.trimOffspring"),sQuery(id+"F0.wireOp",EDGE,"E28.trimOffspring"),sQuery(id+"F0.wireOp",EDGE,"E29.trimOffspring"),sQuery(id+"F0.wireOp",EDGE,"E30.trimOffspring")])],"isStart":false});
            var sketch = newSketch(context, id + "F2", { "sketchPlane" : qUnion([Q0])});
            skCircle(sketch, "E31", {"center": v(0, 0) * mm, "radius": 3.18 * mm});
            skSolve(sketch);
        }
        {
            var Q0;
            Q0 = qSketchRegion(id + "F2", true);
            extrude(context, id + "F3", {"entities" : qUnion([Q0]), "operationType" : NewBodyOperationType.REMOVE, "endBound" : BoundingType.THROUGH_ALL, "oppositeDirection" : true, "depth" : 25.4 * mm});
        }
        {
            var Q0;
            Q0=makeQuery(id+"F1.opExtrude","CAP_FACE",FACE,{"disambiguationData":[OSD([sQuery(id+"F0.wireOp",EDGE,"E0"),sQuery(id+"F0.wireOp",EDGE,"E1"),sQuery(id+"F0.wireOp",EDGE,"E2"),sQuery(id+"F0.wireOp",EDGE,"E3"),sQuery(id+"F0.wireOp",EDGE,"E4.MirrorCS"),sQuery(id+"F0.wireOp",EDGE,"E5.MirrorCS"),sQuery(id+"F0.wireOp",EDGE,"E6.MirrorCS"),sQuery(id+"F0.wireOp",EDGE,"E7.filletArc"),sQuery(id+"F0.wireOp",EDGE,"E8.filletArc"),sQuery(id+"F0.wireOp",EDGE,"E9.filletArc"),sQuery(id+"F0.wireOp",EDGE,"E10.filletArc"),sQuery(id+"F0.wireOp",EDGE,"E11.filletArc"),sQuery(id+"F0.wireOp",EDGE,"E12.filletArc"),sQuery(id+"F0.wireOp",EDGE,"E13.1.0"),sQuery(id+"F0.wireOp",EDGE,"E13.1.1"),sQuery(id+"F0.wireOp",EDGE,"E13.1.2"),sQuery(id+"F0.wireOp",EDGE,"E13.1.3"),sQuery(id+"F0.wireOp",EDGE,"E13.1.4"),sQuery(id+"F0.wireOp",EDGE,"E13.1.5"),sQuery(id+"F0.wireOp",EDGE,"E13.1.6"),sQuery(id+"F0.wireOp",EDGE,"E13.1.7"),sQuery(id+"F0.wireOp",EDGE,"E13.1.8"),sQuery(id+"F0.wireOp",EDGE,"E13.1.9"),sQuery(id+"F0.wireOp",EDGE,"E13.1.10"),sQuery(id+"F0.wireOp",EDGE,"E13.1.11"),sQuery(id+"F0.wireOp",EDGE,"E13.2.0"),sQuery(id+"F0.wireOp",EDGE,"E13.2.1"),sQuery(id+"F0.wireOp",EDGE,"E13.2.2"),sQuery(id+"F0.wireOp",EDGE,"E13.2.3"),sQuery(id+"F0.wireOp",EDGE,"E13.2.4"),sQuery(id+"F0.wireOp",EDGE,"E13.2.5"),sQuery(id+"F0.wireOp",EDGE,"E13.2.6"),sQuery(id+"F0.wireOp",EDGE,"E13.2.7"),sQuery(id+"F0.wireOp",EDGE,"E13.2.8"),sQuery(id+"F0.wireOp",EDGE,"E13.2.9"),sQuery(id+"F0.wireOp",EDGE,"E13.2.10"),sQuery(id+"F0.wireOp",EDGE,"E13.2.11"),sQuery(id+"F0.wireOp",EDGE,"E13.3.0"),sQuery(id+"F0.wireOp",EDGE,"E13.3.1"),sQuery(id+"F0.wireOp",EDGE,"E13.3.2"),sQuery(id+"F0.wireOp",EDGE,"E13.3.3"),sQuery(id+"F0.wireOp",EDGE,"E13.3.4"),sQuery(id+"F0.wireOp",EDGE,"E13.3.5"),sQuery(id+"F0.wireOp",EDGE,"E13.3.6"),sQuery(id+"F0.wireOp",EDGE,"E13.3.7"),sQuery(id+"F0.wireOp",EDGE,"E13.3.8"),sQuery(id+"F0.wireOp",EDGE,"E13.3.9"),sQuery(id+"F0.wireOp",EDGE,"E13.3.10"),sQuery(id+"F0.wireOp",EDGE,"E13.3.11"),sQuery(id+"F0.wireOp",EDGE,"E13.4.0"),sQuery(id+"F0.wireOp",EDGE,"E13.4.1"),sQuery(id+"F0.wireOp",EDGE,"E13.4.2"),sQuery(id+"F0.wireOp",EDGE,"E13.4.3"),sQuery(id+"F0.wireOp",EDGE,"E13.4.4"),sQuery(id+"F0.wireOp",EDGE,"E13.4.5"),sQuery(id+"F0.wireOp",EDGE,"E13.4.6"),sQuery(id+"F0.wireOp",EDGE,"E13.4.7"),sQuery(id+"F0.wireOp",EDGE,"E13.4.8"),sQuery(id+"F0.wireOp",EDGE,"E13.4.9"),sQuery(id+"F0.wireOp",EDGE,"E13.4.10"),sQuery(id+"F0.wireOp",EDGE,"E13.4.11"),sQuery(id+"F0.wireOp",EDGE,"E13.5.0"),sQuery(id+"F0.wireOp",EDGE,"E13.5.1"),sQuery(id+"F0.wireOp",EDGE,"E13.5.2"),sQuery(id+"F0.wireOp",EDGE,"E13.5.3"),sQuery(id+"F0.wireOp",EDGE,"E13.5.4"),sQuery(id+"F0.wireOp",EDGE,"E13.5.5"),sQuery(id+"F0.wireOp",EDGE,"E13.5.6"),sQuery(id+"F0.wireOp",EDGE,"E13.5.7"),sQuery(id+"F0.wireOp",EDGE,"E13.5.8"),sQuery(id+"F0.wireOp",EDGE,"E13.5.9"),sQuery(id+"F0.wireOp",EDGE,"E13.5.10"),sQuery(id+"F0.wireOp",EDGE,"E13.5.11"),sQuery(id+"F0.wireOp",EDGE,"E13.6.0"),sQuery(id+"F0.wireOp",EDGE,"E13.6.1"),sQuery(id+"F0.wireOp",EDGE,"E13.6.2"),sQuery(id+"F0.wireOp",EDGE,"E13.6.3"),sQuery(id+"F0.wireOp",EDGE,"E13.6.4"),sQuery(id+"F0.wireOp",EDGE,"E13.6.5"),sQuery(id+"F0.wireOp",EDGE,"E13.6.6"),sQuery(id+"F0.wireOp",EDGE,"E13.6.7"),sQuery(id+"F0.wireOp",EDGE,"E13.6.8"),sQuery(id+"F0.wireOp",EDGE,"E13.6.9"),sQuery(id+"F0.wireOp",EDGE,"E13.6.10"),sQuery(id+"F0.wireOp",EDGE,"E13.6.11"),sQuery(id+"F0.wireOp",EDGE,"E13.7.0"),sQuery(id+"F0.wireOp",EDGE,"E13.7.1"),sQuery(id+"F0.wireOp",EDGE,"E13.7.2"),sQuery(id+"F0.wireOp",EDGE,"E13.7.3"),sQuery(id+"F0.wireOp",EDGE,"E13.7.4"),sQuery(id+"F0.wireOp",EDGE,"E13.7.5"),sQuery(id+"F0.wireOp",EDGE,"E13.7.6"),sQuery(id+"F0.wireOp",EDGE,"E13.7.7"),sQuery(id+"F0.wireOp",EDGE,"E13.7.8"),sQuery(id+"F0.wireOp",EDGE,"E13.7.9"),sQuery(id+"F0.wireOp",EDGE,"E13.7.10"),sQuery(id+"F0.wireOp",EDGE,"E13.7.11"),sQuery(id+"F0.wireOp",EDGE,"E13.8.0"),sQuery(id+"F0.wireOp",EDGE,"E13.8.1"),sQuery(id+"F0.wireOp",EDGE,"E13.8.2"),sQuery(id+"F0.wireOp",EDGE,"E13.8.3"),sQuery(id+"F0.wireOp",EDGE,"E13.8.4"),sQuery(id+"F0.wireOp",EDGE,"E13.8.5"),sQuery(id+"F0.wireOp",EDGE,"E13.8.6"),sQuery(id+"F0.wireOp",EDGE,"E13.8.7"),sQuery(id+"F0.wireOp",EDGE,"E13.8.8"),sQuery(id+"F0.wireOp",EDGE,"E13.8.9"),sQuery(id+"F0.wireOp",EDGE,"E13.8.10"),sQuery(id+"F0.wireOp",EDGE,"E13.8.11"),sQuery(id+"F0.wireOp",EDGE,"E13.9.0"),sQuery(id+"F0.wireOp",EDGE,"E13.9.1"),sQuery(id+"F0.wireOp",EDGE,"E13.9.2"),sQuery(id+"F0.wireOp",EDGE,"E13.9.3"),sQuery(id+"F0.wireOp",EDGE,"E13.9.4"),sQuery(id+"F0.wireOp",EDGE,"E13.9.5"),sQuery(id+"F0.wireOp",EDGE,"E13.9.6"),sQuery(id+"F0.wireOp",EDGE,"E13.9.7"),sQuery(id+"F0.wireOp",EDGE,"E13.9.8"),sQuery(id+"F0.wireOp",EDGE,"E13.9.9"),sQuery(id+"F0.wireOp",EDGE,"E13.9.10"),sQuery(id+"F0.wireOp",EDGE,"E13.9.11"),sQuery(id+"F0.wireOp",EDGE,"E13.10.0"),sQuery(id+"F0.wireOp",EDGE,"E13.10.1"),sQuery(id+"F0.wireOp",EDGE,"E13.10.2"),sQuery(id+"F0.wireOp",EDGE,"E13.10.3"),sQuery(id+"F0.wireOp",EDGE,"E13.10.4"),sQuery(id+"F0.wireOp",EDGE,"E13.10.5"),sQuery(id+"F0.wireOp",EDGE,"E13.10.6"),sQuery(id+"F0.wireOp",EDGE,"E13.10.7"),sQuery(id+"F0.wireOp",EDGE,"E13.10.8"),sQuery(id+"F0.wireOp",EDGE,"E13.10.9"),sQuery(id+"F0.wireOp",EDGE,"E13.10.10"),sQuery(id+"F0.wireOp",EDGE,"E13.10.11"),sQuery(id+"F0.wireOp",EDGE,"E13.11.0"),sQuery(id+"F0.wireOp",EDGE,"E13.11.1"),sQuery(id+"F0.wireOp",EDGE,"E13.11.2"),sQuery(id+"F0.wireOp",EDGE,"E13.11.3"),sQuery(id+"F0.wireOp",EDGE,"E13.11.4"),sQuery(id+"F0.wireOp",EDGE,"E13.11.5"),sQuery(id+"F0.wireOp",EDGE,"E13.11.6"),sQuery(id+"F0.wireOp",EDGE,"E13.11.7"),sQuery(id+"F0.wireOp",EDGE,"E13.11.8"),sQuery(id+"F0.wireOp",EDGE,"E13.11.9"),sQuery(id+"F0.wireOp",EDGE,"E13.11.10"),sQuery(id+"F0.wireOp",EDGE,"E13.11.11"),sQuery(id+"F0.wireOp",EDGE,"E13.12.0"),sQuery(id+"F0.wireOp",EDGE,"E13.12.1"),sQuery(id+"F0.wireOp",EDGE,"E13.12.2"),sQuery(id+"F0.wireOp",EDGE,"E13.12.3"),sQuery(id+"F0.wireOp",EDGE,"E13.12.4"),sQuery(id+"F0.wireOp",EDGE,"E13.12.5"),sQuery(id+"F0.wireOp",EDGE,"E13.12.6"),sQuery(id+"F0.wireOp",EDGE,"E13.12.7"),sQuery(id+"F0.wireOp",EDGE,"E13.12.8"),sQuery(id+"F0.wireOp",EDGE,"E13.12.9"),sQuery(id+"F0.wireOp",EDGE,"E13.12.10"),sQuery(id+"F0.wireOp",EDGE,"E13.12.11"),sQuery(id+"F0.wireOp",EDGE,"E13.13.0"),sQuery(id+"F0.wireOp",EDGE,"E13.13.1"),sQuery(id+"F0.wireOp",EDGE,"E13.13.2"),sQuery(id+"F0.wireOp",EDGE,"E13.13.3"),sQuery(id+"F0.wireOp",EDGE,"E13.13.4"),sQuery(id+"F0.wireOp",EDGE,"E13.13.5"),sQuery(id+"F0.wireOp",EDGE,"E13.13.6"),sQuery(id+"F0.wireOp",EDGE,"E13.13.7"),sQuery(id+"F0.wireOp",EDGE,"E13.13.8"),sQuery(id+"F0.wireOp",EDGE,"E13.13.9"),sQuery(id+"F0.wireOp",EDGE,"E13.13.10"),sQuery(id+"F0.wireOp",EDGE,"E13.13.11"),sQuery(id+"F0.wireOp",EDGE,"E13.14.0"),sQuery(id+"F0.wireOp",EDGE,"E13.14.1"),sQuery(id+"F0.wireOp",EDGE,"E13.14.2"),sQuery(id+"F0.wireOp",EDGE,"E13.14.3"),sQuery(id+"F0.wireOp",EDGE,"E13.14.4"),sQuery(id+"F0.wireOp",EDGE,"E13.14.5"),sQuery(id+"F0.wireOp",EDGE,"E13.14.6"),sQuery(id+"F0.wireOp",EDGE,"E13.14.7"),sQuery(id+"F0.wireOp",EDGE,"E13.14.8"),sQuery(id+"F0.wireOp",EDGE,"E13.14.9"),sQuery(id+"F0.wireOp",EDGE,"E13.14.10"),sQuery(id+"F0.wireOp",EDGE,"E13.14.11"),sQuery(id+"F0.wireOp",EDGE,"E13.15.0"),sQuery(id+"F0.wireOp",EDGE,"E13.15.1"),sQuery(id+"F0.wireOp",EDGE,"E13.15.2"),sQuery(id+"F0.wireOp",EDGE,"E13.15.3"),sQuery(id+"F0.wireOp",EDGE,"E13.15.4"),sQuery(id+"F0.wireOp",EDGE,"E13.15.5"),sQuery(id+"F0.wireOp",EDGE,"E13.15.6"),sQuery(id+"F0.wireOp",EDGE,"E13.15.7"),sQuery(id+"F0.wireOp",EDGE,"E13.15.8"),sQuery(id+"F0.wireOp",EDGE,"E13.15.9"),sQuery(id+"F0.wireOp",EDGE,"E13.15.10"),sQuery(id+"F0.wireOp",EDGE,"E13.15.11"),sQuery(id+"F0.wireOp",EDGE,"E13.16.0"),sQuery(id+"F0.wireOp",EDGE,"E13.16.1"),sQuery(id+"F0.wireOp",EDGE,"E13.16.2"),sQuery(id+"F0.wireOp",EDGE,"E13.16.3"),sQuery(id+"F0.wireOp",EDGE,"E13.16.4"),sQuery(id+"F0.wireOp",EDGE,"E13.16.5"),sQuery(id+"F0.wireOp",EDGE,"E13.16.6"),sQuery(id+"F0.wireOp",EDGE,"E13.16.7"),sQuery(id+"F0.wireOp",EDGE,"E13.16.8"),sQuery(id+"F0.wireOp",EDGE,"E13.16.9"),sQuery(id+"F0.wireOp",EDGE,"E13.16.10"),sQuery(id+"F0.wireOp",EDGE,"E13.16.11"),sQuery(id+"F0.wireOp",EDGE,"E13.17.0"),sQuery(id+"F0.wireOp",EDGE,"E13.17.1"),sQuery(id+"F0.wireOp",EDGE,"E13.17.2"),sQuery(id+"F0.wireOp",EDGE,"E13.17.3"),sQuery(id+"F0.wireOp",EDGE,"E13.17.4"),sQuery(id+"F0.wireOp",EDGE,"E13.17.5"),sQuery(id+"F0.wireOp",EDGE,"E13.17.6"),sQuery(id+"F0.wireOp",EDGE,"E13.17.7"),sQuery(id+"F0.wireOp",EDGE,"E13.17.8"),sQuery(id+"F0.wireOp",EDGE,"E13.17.9"),sQuery(id+"F0.wireOp",EDGE,"E13.17.10"),sQuery(id+"F0.wireOp",EDGE,"E13.17.11"),sQuery(id+"F0.wireOp",EDGE,"E14.trimOffspring"),sQuery(id+"F0.wireOp",EDGE,"E15.trimOffspring"),sQuery(id+"F0.wireOp",EDGE,"E16.trimOffspring"),sQuery(id+"F0.wireOp",EDGE,"E17.trimOffspring"),sQuery(id+"F0.wireOp",EDGE,"E18.trimOffspring"),sQuery(id+"F0.wireOp",EDGE,"E19.trimOffspring"),sQuery(id+"F0.wireOp",EDGE,"E20.trimOffspring"),sQuery(id+"F0.wireOp",EDGE,"E21.trimOffspring"),sQuery(id+"F0.wireOp",EDGE,"E22.trimOffspring"),sQuery(id+"F0.wireOp",EDGE,"E23.trimOffspring"),sQuery(id+"F0.wireOp",EDGE,"E24.trimOffspring"),sQuery(id+"F0.wireOp",EDGE,"E25.trimOffspring"),sQuery(id+"F0.wireOp",EDGE,"E26.trimOffspring"),sQuery(id+"F0.wireOp",EDGE,"E27.trimOffspring"),sQuery(id+"F0.wireOp",EDGE,"E28.trimOffspring"),sQuery(id+"F0.wireOp",EDGE,"E29.trimOffspring"),sQuery(id+"F0.wireOp",EDGE,"E30.trimOffspring")])],"isStart":false});
            shell(context, id + "F4", {"entities" : qUnion([Q0]), "thickness" : 5.08 * mm});
        }
        {
            var Q0;
            Q0=qCreatedBy(makeId("Right.planeOp"),FACE);
            var sketch = newSketch(context, id + "F5", { "sketchPlane" : qUnion([Q0])});
            skCircle(sketch, "E32", {"center": v(-9.53, 0) * mm, "radius": 1.13 * mm});
            skSolve(sketch);
        }
        {
            var Q0;
            Q0 = qSketchRegion(id + "F5", true);
            extrude(context, id + "F6", {"entities" : qUnion([Q0]), "operationType" : NewBodyOperationType.REMOVE, "oppositeDirection" : true, "depth" : 9.52 * mm});
        }
    });
